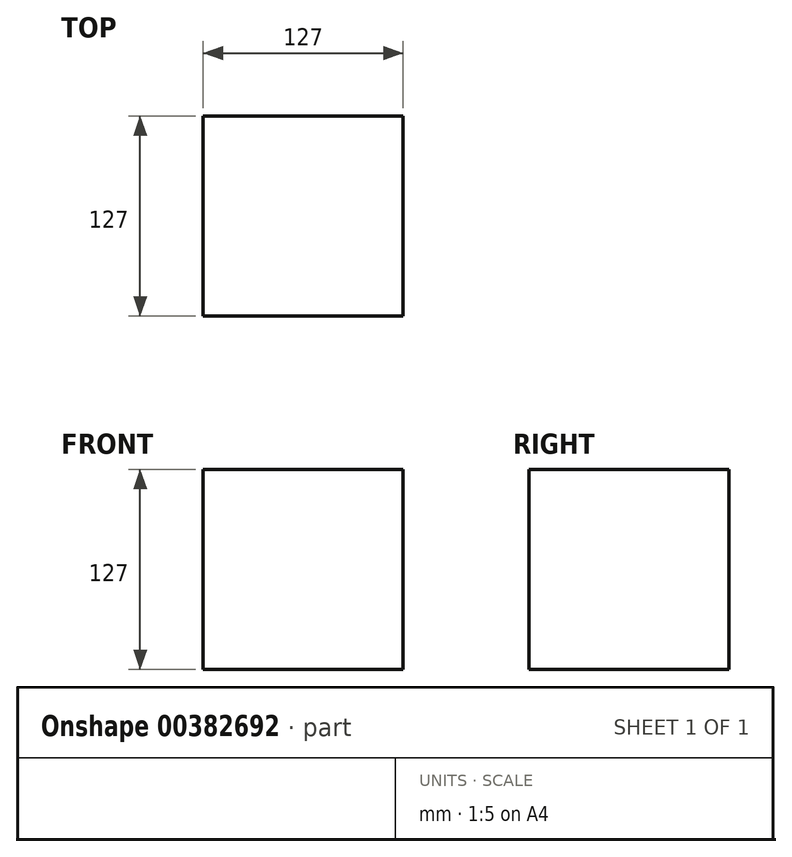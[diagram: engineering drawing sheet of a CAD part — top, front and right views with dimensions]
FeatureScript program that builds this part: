
annotation { "Feature Type Name" : "Feature", "Feature Type Description" : "" }
export const myFeature = defineFeature(function(context is Context, id is Id, definition is map)
    precondition{}
    {
        {
            var Q0;
            Q0=qCreatedBy(makeId("Front.planeOp"),FACE);
            var sketch = newSketch(context, id + "F0", { "sketchPlane" : qUnion([Q0])});
            skLineSegment(sketch, "E0", {"start": v(-127, 127) * mm, "end": v(-127, 0) * mm});
            skLineSegment(sketch, "E1", {"start": v(-127, 0) * mm, "end": v(0, 0) * mm});
            skLineSegment(sketch, "E2", {"start": v(0, 0) * mm, "end": v(0, 127) * mm});
            skLineSegment(sketch, "E3", {"start": v(0, 127) * mm, "end": v(-127, 127) * mm});
            skSolve(sketch);
        }
        {
            var Q0;
            Q0 = qSketchRegion(id + "F0", true);
            extrude(context, id + "F1", {"entities" : qUnion([Q0]), "depth" : 127 * mm});
        }
    });
